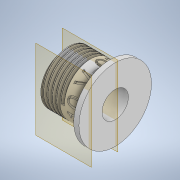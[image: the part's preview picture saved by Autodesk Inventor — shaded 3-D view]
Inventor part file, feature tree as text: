
AUTODESK INVENTOR PART (.ipt)
format: ipt  version: 2021.1 (Build 251245010, 245A)  size: 791,552 bytes
history: native  units: in
note: dims shown in document units (in); Inventor stores cm internally (conversion verified against a paired STEP export)
features: sketch x3, revolve x1, helix x1, plane x1, emboss x1
ambient origin geometry x8: Origin, YZ Plane, XZ Plane, XY Plane, X Axis, Y Axis, Z Axis, Center Point
bodies: Solid1 (feature_tree)
feature tree (7):
  revolve  "Revolution1"  [1 undecoded]
  helix  "Coil1"  [1 undecoded]
  plane  "Work Plane1"
  emboss  "Emboss1"
  sketch  "Sketch2"  dims[d0=0.825in d1=0.3in d2=0.118in]
  sketch  "Sketch4"  dims[d3=0.75in]
  sketch  "Sketch5"  dims[d4=90.0deg d5=0.6in d6=0.25in d10=60.0deg d11=0.0097in d12=60.0deg d13=60.0deg d15=0.1in d16=0.2in d17=0.05in d18=0.6042in d19=0.542in d20=30.0deg d21=0.1in d22=0.625in d23=0.3937in d24=0.0in d25=90.0deg d26=90.0deg d27=0.0in d28=0.0in d35=0.2in d36=0.05in d37=0.0in]
note: 2 required parameter values undecoded (feature->parameter linkage not recoverable at this tier; creation-order binding heuristic only, values carry confidence <= 0.55)